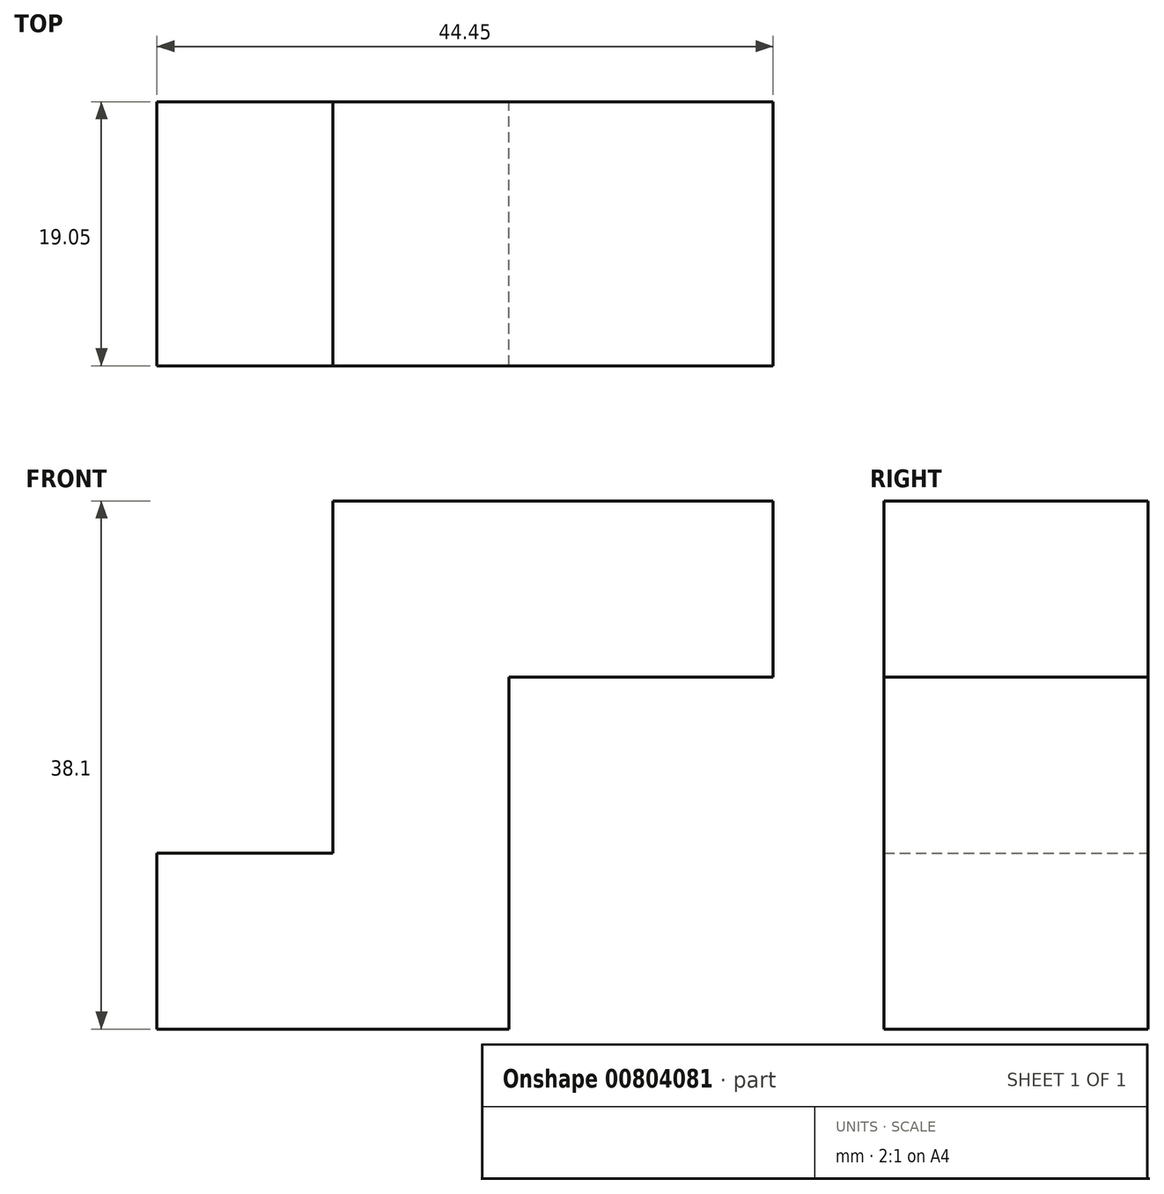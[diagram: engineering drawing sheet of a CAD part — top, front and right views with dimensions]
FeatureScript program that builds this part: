
annotation { "Feature Type Name" : "Feature", "Feature Type Description" : "" }
export const myFeature = defineFeature(function(context is Context, id is Id, definition is map)
    precondition{}
    {
        {
            var Q0;
            Q0=qCreatedBy(makeId("Front.planeOp"),FACE);
            var sketch = newSketch(context, id + "F0", { "sketchPlane" : qUnion([Q0])});
            skLineSegment(sketch, "E0", {"start": v(0, 0) * mm, "end": v(25.4, 0) * mm});
            skLineSegment(sketch, "E1", {"start": v(25.4, 0) * mm, "end": v(25.4, 25.4) * mm});
            skLineSegment(sketch, "E2", {"start": v(25.4, 25.4) * mm, "end": v(44.45, 25.4) * mm});
            skLineSegment(sketch, "E3", {"start": v(44.45, 25.4) * mm, "end": v(44.45, 38.1) * mm});
            skLineSegment(sketch, "E4", {"start": v(44.45, 38.1) * mm, "end": v(12.7, 38.1) * mm});
            skLineSegment(sketch, "E5", {"start": v(12.7, 38.1) * mm, "end": v(12.7, 12.7) * mm});
            skLineSegment(sketch, "E6", {"start": v(12.7, 12.7) * mm, "end": v(0, 12.7) * mm});
            skLineSegment(sketch, "E7", {"start": v(0, 12.7) * mm, "end": v(0, 0) * mm});
            skSolve(sketch);
        }
        {
            var Q0;
            Q0=makeQuery(id+"F0.imprint","IMPRINT",FACE,{"disambiguationData":[TD([[makeQuery(id+"F0.imprint","IMPRINT",EDGE,{"derivedFrom":sQuery(id+"F0.wireOp",EDGE,"E0")}),1.0]])]});
            extrude(context, id + "F1", {"entities" : qUnion([Q0]), "depth" : 19.05 * mm, "offsetDistance" : 25.4 * mm});
        }
    });
